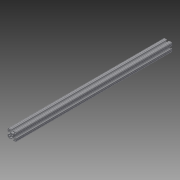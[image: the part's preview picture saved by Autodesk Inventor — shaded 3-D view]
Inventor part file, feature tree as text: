
AUTODESK INVENTOR PART (.ipt)
format: ipt  version: 2013 (Build 170138000, 138)  size: 295,424 bytes
history: native  units: in
note: dims shown in document units (in); Inventor stores cm internally (conversion verified against a paired STEP export)
features: extrude x1, sketch x1
ambient origin geometry x8: Origin, YZ Plane, XZ Plane, XY Plane, X Axis, Y Axis, Z Axis, Center Point
bodies: Solid1 (feature_tree)
feature tree (2):
  extrude  "Extrusion1"  [1 undecoded]
  sketch  "Sketch1"  dims[d0=28.0in d1=0.0in]
note: 1 required parameter value undecoded (feature->parameter linkage not recoverable at this tier; creation-order binding heuristic only, values carry confidence <= 0.55)
